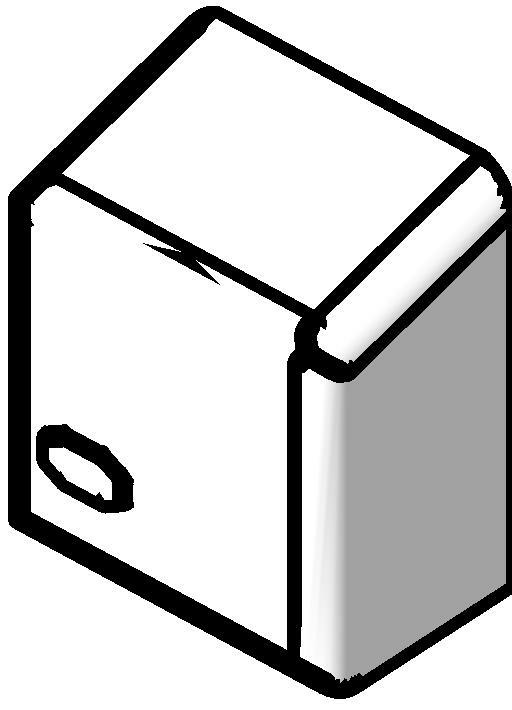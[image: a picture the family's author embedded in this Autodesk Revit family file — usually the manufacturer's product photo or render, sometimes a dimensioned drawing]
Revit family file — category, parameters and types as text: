
# Revit family: Deca_Válvula para mictorio acionamento com sensor bivolt_Decalux_2580
name_source: partatom
category: Plumbing Fixtures
units: mm (PartAtom-declared; Revit-internal decimal feet)

## family parameters
Cut with Voids When Loaded = No
Host = Face
Part Type = Normal
Room Calculation Point = No
Round Connector Dimension = Use Radius
Shared = No

## types (1)
- 2580.E.BR_Branco_DN15
    Acompanha o Produto = Acompanha Flexivel; parafusos e buchas para fixação, Fonte Bivolt
    Aprovado por = quattroD
    Atendimento ao Cliente = 0800-0117073
    CWFU = 0
    Categoria = SISTEMAS DE DESCARGA
    Composição Anel Vedação = -
    Composição Assento = -
    Composição Básica = Liga de Cobre (bronze e latão),Plásticos de Engenharia,Elastômeros,Eletrônicos
    Composição Componente = -
    Consumo = 8 l/min
    Cor Interna = -
    Cor Principal = Branco
    Cor Secundária = -
    Cores Componente = -
    Criado por = quattroD
    Código Pai = 2580
    Default Elevation = 1100 mm
    Description = Válvula de mictório acionamento com sensor bivolt
    Diâmetro Água Fria = 15 mm  [stored 0.0492126 ft]
    Diâmetro Água Fria Saída = 15 mm  [stored 0.0492126 ft]
    HWFU = 0
    Informações Complementares = -
    Itens de Instalação = -
    Linha = Decalux
    Manufacturer = Deca
    Material = Deca_Branco
    Model = 2580.E.BR
    Norma = NBR9050
    Peso Líquido (Kg) = 0.732
    Pressão máx. funcionamento = 40 MCA
    Pressão mín. Aquec. Acúmulo = -
    Pressão mín. Aquec. Passagem = -
    Pressão mín. funcionamento = 2 MCA
    Raio Água Fria = 8 mm  [stored 0.0262467 ft]
    Raio Água Fria Saída = 8 mm  [stored 0.0262467 ft]
    Saída de Esgoto = -
    Segmento = Banheiro Médio
    Tipo de dispositivo economizador = Sim
    Tipo de mecanismo utilizado = -
    Tipo de rosca de entrada = BSP NBR 8133
    Tipo de rosca de saída = BSP NBR 8133
    URL = www.deca.com.br
    Vazão na Pressão máx. (L/min) = 8
    Vazão na Pressão mín. (L/min) = 5

note: source unit labels omitted for Vazão na Pressão máx. (L/min), Vazão na Pressão mín. (L/min) — the stored unit's dimension contradicts the parameter name (converter mislabeling)

note: [stored X ft] marks values corroborated as IEEE doubles in the binary element streams (Revit-internal decimal feet)

## geometry (parser evidence)
native form markers: Sweep x2
no freeform markers — native parametric forms only
